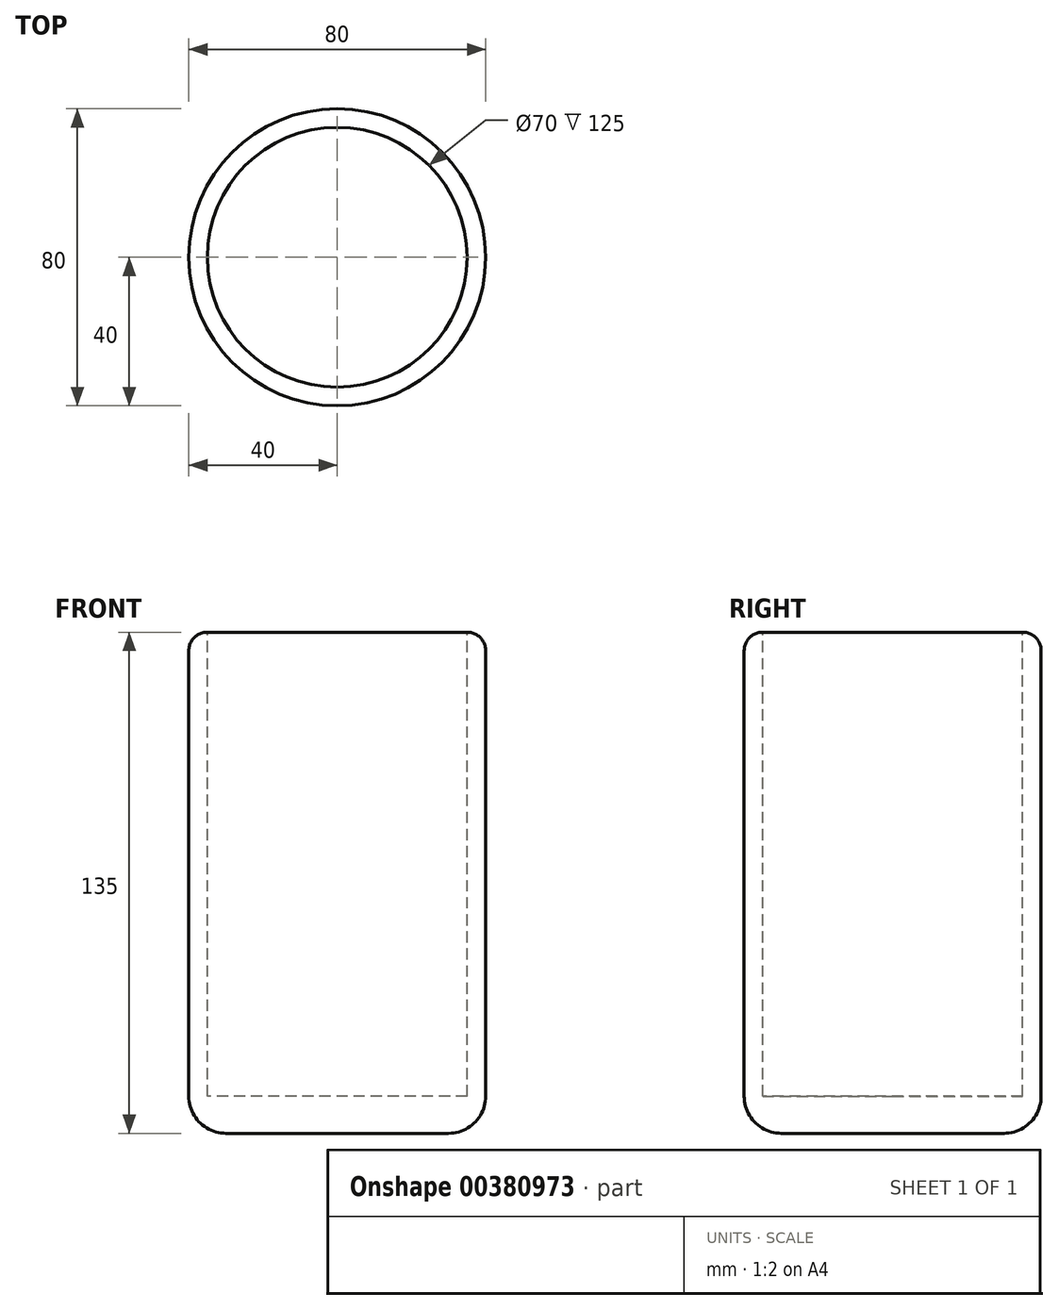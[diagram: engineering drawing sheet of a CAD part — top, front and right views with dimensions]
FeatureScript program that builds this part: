
annotation { "Feature Type Name" : "Feature", "Feature Type Description" : "" }
export const myFeature = defineFeature(function(context is Context, id is Id, definition is map)
    precondition{}
    {
        {
            var Q0;
            Q0=qCreatedBy(makeId("Front.planeOp"),FACE);
            var sketch = newSketch(context, id + "F0", { "sketchPlane" : qUnion([Q0])});
            skLineSegment(sketch, "E0.bottom", {"start": v(0, 0) * mm, "end": v(40, 0) * mm});
            skLineSegment(sketch, "E0.right", {"start": v(40, 0) * mm, "end": v(40, 135) * mm});
            skLineSegment(sketch, "E1.bottom", {"start": v(0, 0) * mm, "end": v(35, 0) * mm});
            skLineSegment(sketch, "E1.right", {"start": v(35, 0) * mm, "end": v(35, 135) * mm});
            skLineSegment(sketch, "E2", {"start": v(0, 10) * mm, "end": v(40, 10) * mm});
            skLineSegment(sketch, "E3", {"start": v(0, 10) * mm, "end": v(0, 0) * mm});
            skLineSegment(sketch, "E4", {"start": v(35, 135) * mm, "end": v(40, 135) * mm});
            skSolve(sketch);
        }
        {
            var Q0;
            {var subQ0=sQuery(id+"F0.wireOp",EDGE,"E1.bottom");Q0=makeQuery(id+"F0.imprint","IMPRINT",FACE,{"disambiguationData":[TD([[makeQuery(id+"F0.imprint","IMPRINT",EDGE,{"derivedFrom":subQ0}),1.0]])]});}
            var Q1;
            {var subQ0=sQuery(id+"F0.wireOp",EDGE,"E0.bottom");Q1=makeQuery(id+"F0.imprint","IMPRINT",FACE,{"disambiguationData":[TD([[makeQuery(id+"F0.imprint","IMPRINT",EDGE,{"derivedFrom":subQ0}),1.0]])]});}
            var Q2;
            {var subQ0=sQuery(id+"F0.wireOp",EDGE,"E4");Q2=makeQuery(id+"F0.imprint","IMPRINT",FACE,{"disambiguationData":[TD([[makeQuery(id+"F0.imprint","IMPRINT",EDGE,{"derivedFrom":subQ0}),-1.0]])]});}
            var Q3;
            Q3=sQuery(id+"F0.wireOp",EDGE,"E3");
            revolve(context, id + "F1", {"entities" : qUnion([Q0, Q1, Q2]), "axis" : qUnion([Q3]), "revolveType" : RevolveType.FULL});
        }
        {
            var Q0;
            Q0=makeQuery(id+"F1.opRevolve","SWEPT_EDGE",EDGE,{"disambiguationData":[OSD([sQuery(id+"F0.wireOp",EDGE,"E0.right"),sQuery(id+"F0.wireOp",EDGE,"E4")])]});
            fillet(context, id + "F2", {"entities" : qUnion([Q0]), "radius" : 5 * mm, "tangentPropagation" : true, "allowEdgeOverflow" : false});
        }
        {
            var Q0;
            Q0=makeQuery(id+"F1.opRevolve","SWEPT_EDGE",EDGE,{"disambiguationData":[OSD([sQuery(id+"F0.wireOp",EDGE,"E0.bottom"),sQuery(id+"F0.wireOp",EDGE,"E0.right")])]});
            fillet(context, id + "F3", {"entities" : qUnion([Q0]), "radius" : 10 * mm, "tangentPropagation" : true, "allowEdgeOverflow" : false});
        }
    });
